# Revit family: HL_Трап для балконов и террас_HL5100TK
name_source: partatom
category: Instalační zařizovací předměty
revit_build: Autodesk Revit 2016 (Build: 20151007_0715(x64)
units: mm (PartAtom-declared; Revit-internal decimal feet)

## family parameters
Bod výpočtu místnosti = Ano
Kóta kulaté spojky = Použít průměr
Nadpis OmniClass = Deck Waste Water Drains
Ořezat dutým tvarem při načtení = Ne
Sdílené = Ne
Typ součásti = Normální
Vždy vertikální = Ano
Založené na pracovní rovině = Ne
Číslo OmniClass = 23.70.50.21.24.14

## types (1)
- HL_Трап для балконов и террас_HL5100TK
    EAN = 9003076034727
    Klíčová poznámka = HL5100TK
    Komentáře k typům = Корпус для трапов для внутренних помещений DN75 горизонтальный
    Model = HL5100TK
    Popis = Трап для балконов и террас
    Připojení CW = Ne
    Připojení HW = Ne
    Připojení odpadu = Ano
    Připojení ventilace = Ne
    URL = https://www.hutterer-lechner.com
    Výrobce = HL Hutterer & Lechner GmbH
    ВЕС = 0,54 kg
    ВЫСОТА МОНТАЖА = 102mm
    МАТЕРИАЛ = PP
    НОМИНАЛЬНЫЙ ДИАМЕТР = 75 mm
    РАЗМЕР = DN 75
    Угол установки = 90.00°

## geometry (parser evidence)
native form markers: Blend x6, Sweep x31
no freeform markers — native parametric forms only
